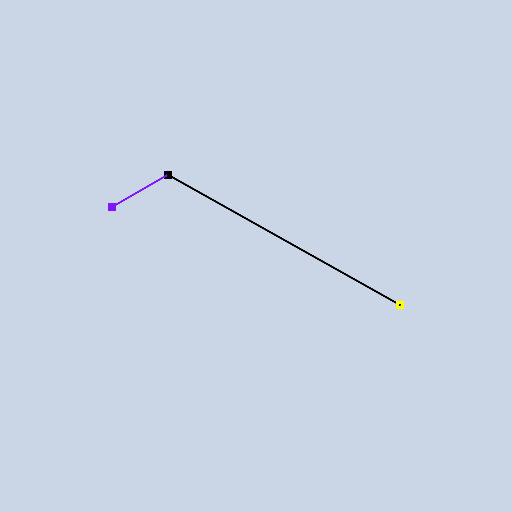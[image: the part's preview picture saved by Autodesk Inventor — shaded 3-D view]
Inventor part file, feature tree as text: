
AUTODESK INVENTOR PART (.ipt)
format: ipt  version: 2025 (Build 290162000, 162)  size: 90,624 bytes
history: native  units: in
note: dims shown in document units (in); Inventor stores cm internally (conversion verified against a paired STEP export)
features: other x2, plane x1, sketch x1
ambient origin geometry x8: Origin, YZ Plane, XZ Plane, XY Plane, X Axis, Y Axis, Z Axis, Center Point
feature tree (4):
  other  "Work Point1"
  other  "Work Point2"
  plane  "Work Plane1"
  sketch  "3D Sketch1"
